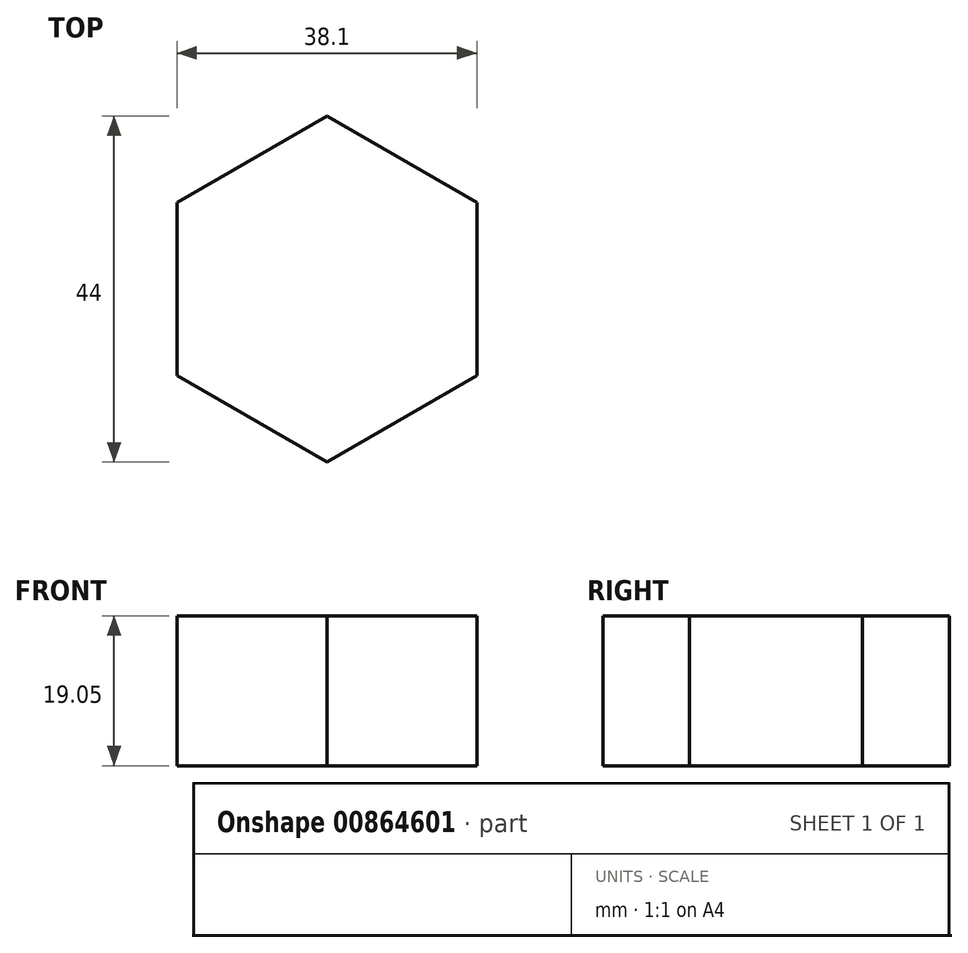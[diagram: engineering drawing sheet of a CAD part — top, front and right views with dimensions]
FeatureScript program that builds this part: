
annotation { "Feature Type Name" : "Feature", "Feature Type Description" : "" }
export const myFeature = defineFeature(function(context is Context, id is Id, definition is map)
    precondition{}
    {
        {
            var Q0;
            Q0=qCreatedBy(makeId("Top.planeOp"),FACE);
            var sketch = newSketch(context, id + "F0", { "sketchPlane" : qUnion([Q0])});
            skCircle(sketch, "E0.cCircle", {"center": v(0, 0) * mm, "radius": 19.05 * mm, "construction": true});
            skLineSegment(sketch, "E0.0", {"start": v(19.05, 11) * mm, "end": v(19.05, -11) * mm});
            skLineSegment(sketch, "E0.1", {"start": v(19.05, -11) * mm, "end": v(0, -22) * mm});
            skLineSegment(sketch, "E0.2", {"start": v(0, -22) * mm, "end": v(-19.05, -11) * mm});
            skLineSegment(sketch, "E0.3", {"start": v(-19.05, -11) * mm, "end": v(-19.05, 11) * mm});
            skLineSegment(sketch, "E0.4", {"start": v(-19.05, 11) * mm, "end": v(0, 22) * mm});
            skLineSegment(sketch, "E0.5", {"start": v(0, 22) * mm, "end": v(19.05, 11) * mm});
            skPoint(sketch, "E0.0.midPoint", {"position": v(19.05, 0) * mm});
            skSolve(sketch);
        }
        {
            var Q0;
            Q0 = qSketchRegion(id + "F0", true);
            extrude(context, id + "F1", {"entities" : qUnion([Q0]), "depth" : 19.05 * mm, "offsetDistance" : 25.4 * mm});
        }
    });
